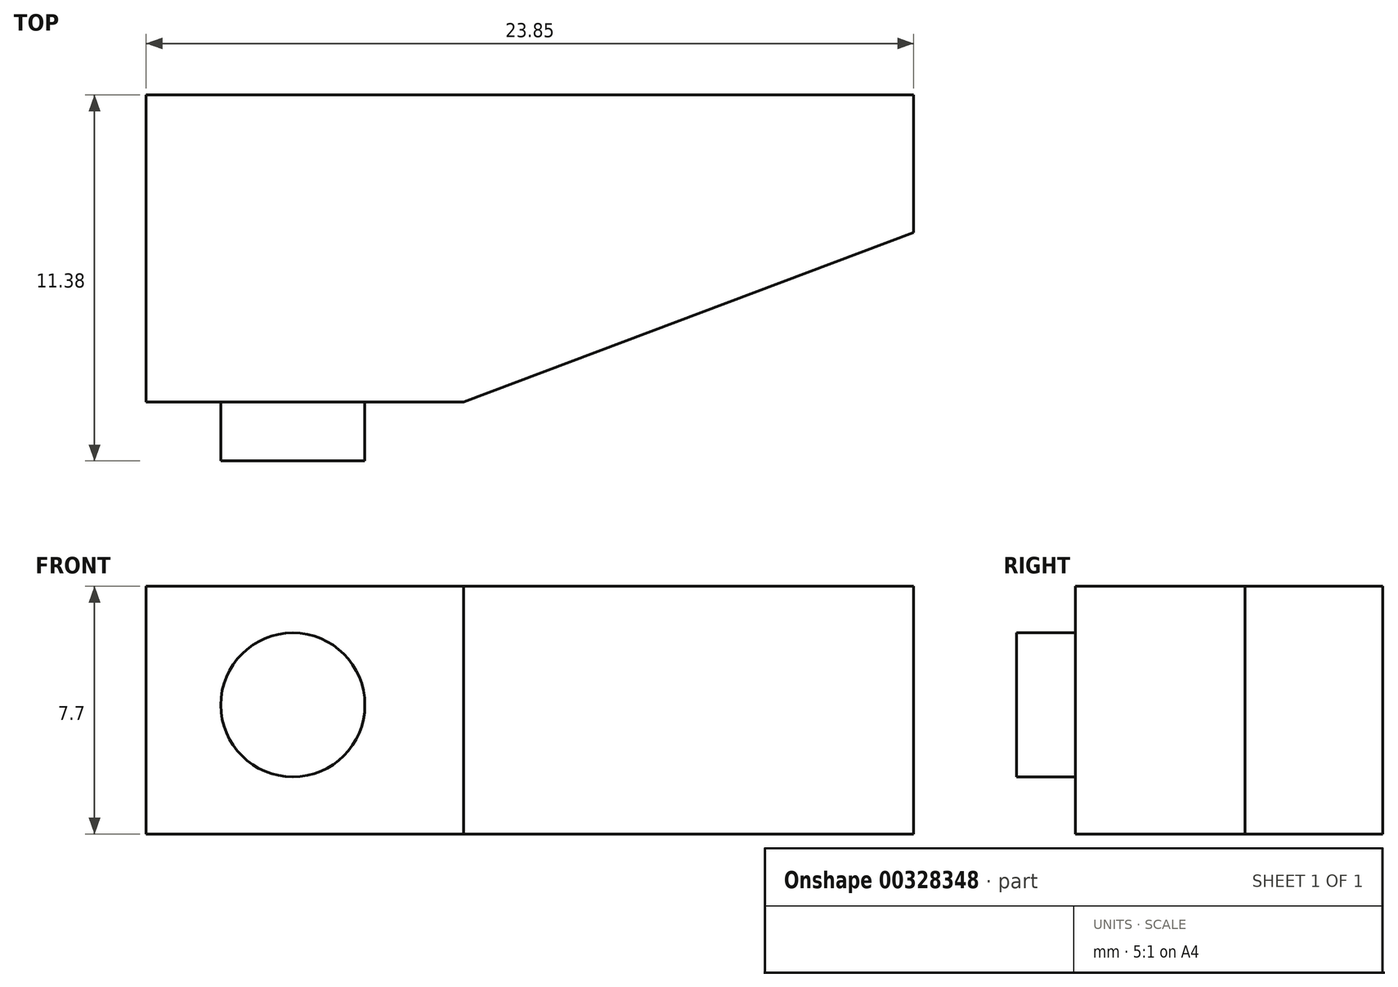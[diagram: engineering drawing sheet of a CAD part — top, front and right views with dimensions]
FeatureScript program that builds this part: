
annotation { "Feature Type Name" : "Feature", "Feature Type Description" : "" }
export const myFeature = defineFeature(function(context is Context, id is Id, definition is map)
    precondition{}
    {
        {
            var Q0;
            Q0=qCreatedBy(makeId("Top.planeOp"),FACE);
            var sketch = newSketch(context, id + "F0", { "sketchPlane" : qUnion([Q0])});
            skLineSegment(sketch, "E0", {"start": v(0, 0) * mm, "end": v(-23.85, 0) * mm});
            skLineSegment(sketch, "E1", {"start": v(-23.85, 0) * mm, "end": v(-23.85, -9.55) * mm});
            skLineSegment(sketch, "E2", {"start": v(-23.85, -9.55) * mm, "end": v(-13.99, -9.55) * mm});
            skLineSegment(sketch, "E3", {"start": v(-13.99, -9.55) * mm, "end": v(0, -4.28) * mm});
            skLineSegment(sketch, "E4", {"start": v(0, -4.28) * mm, "end": v(0, 0) * mm});
            skSolve(sketch);
        }
        {
            var Q0;
            Q0=makeQuery(id+"F0.imprint","IMPRINT",FACE,{"disambiguationData":[TD([[makeQuery(id+"F0.imprint","IMPRINT",EDGE,{"derivedFrom":sQuery(id+"F0.wireOp",EDGE,"E0")}),1.0]])]});
            extrude(context, id + "F1", {"entities" : qUnion([Q0]), "depth" : 7.7 * mm});
        }
        {
            var Q0;
            Q0=makeQuery(id+"F1.opExtrude","SWEPT_FACE",FACE,{"disambiguationData":[OSD([sQuery(id+"F0.wireOp",EDGE,"E2")])]});
            var sketch = newSketch(context, id + "F2", { "sketchPlane" : qUnion([Q0])});
            skSolve(sketch);
        }
        {
            var Q0;
            {var subQ0=sQuery(id+"F0.wireOp",EDGE,"E2");Q0=makeQuery(id+"F2.imprint","IMPRINT",FACE,{"disambiguationData":[TD([[makeQuery(id+"F2.imprint","IMPRINT",EDGE,{"derivedFrom":makeQuery(id+"F1.opExtrude","CAP_EDGE",EDGE,{"disambiguationData":[OSD([subQ0])],"isStart":true})}),1.0]])]});}
            var sketch = newSketch(context, id + "F3", { "sketchPlane" : qUnion([Q0])});
            skCircle(sketch, "E5", {"center": v(-19.3, 4.01) * mm, "radius": 2.24 * mm});
            skSolve(sketch);
        }
        {
            var Q0;
            Q0 = qSketchRegion(id + "F3", true);
            extrude(context, id + "F4", {"entities" : qUnion([Q0]), "operationType" : NewBodyOperationType.ADD, "depth" : 1.83 * mm});
        }
    });
